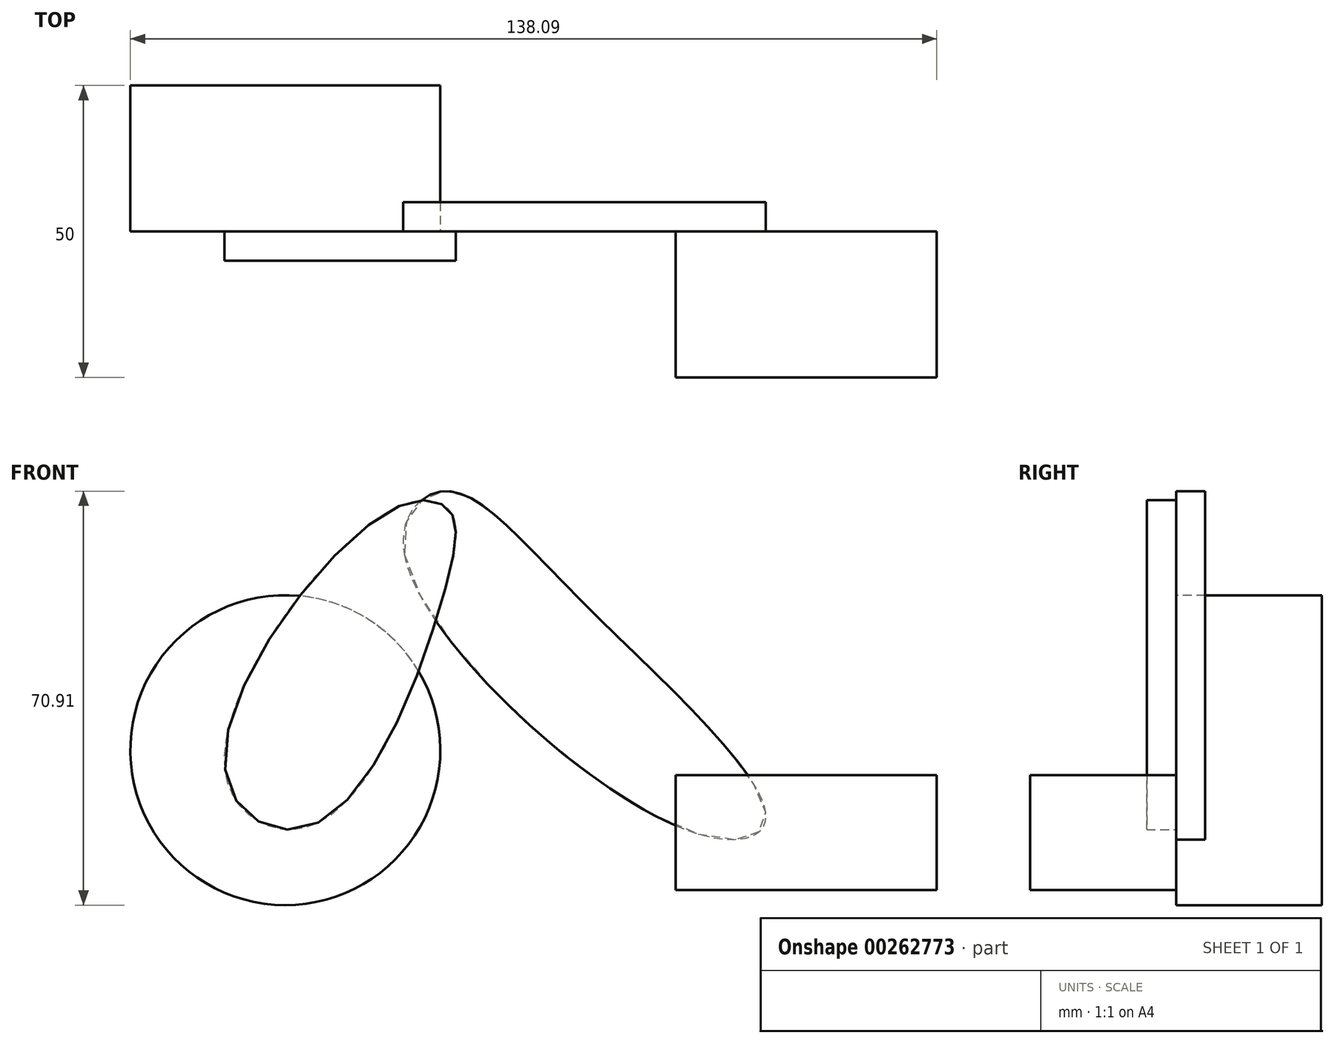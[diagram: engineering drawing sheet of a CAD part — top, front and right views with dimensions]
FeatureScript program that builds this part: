
annotation { "Feature Type Name" : "Feature", "Feature Type Description" : "" }
export const myFeature = defineFeature(function(context is Context, id is Id, definition is map)
    precondition{}
    {
        {
            var Q0;
            Q0=qCreatedBy(makeId("Front.planeOp"),FACE);
            var sketch = newSketch(context, id + "F0", { "sketchPlane" : qUnion([Q0])});
            skCircle(sketch, "E0", {"center": v(0, 0) * mm, "radius": 26.54 * mm});
            skSolve(sketch);
        }
        {
            var Q0;
            Q0=qCreatedBy(makeId("Front.planeOp"),FACE);
            var sketch = newSketch(context, id + "F1", { "sketchPlane" : qUnion([Q0])});
            skFitSpline(sketch, "E1", {"points": [v(-10.32, -3.32) * mm, v(17.7, 40.91) * mm, v(28.01, 41.16) * mm, v(27.77, 29.12) * mm, v(5.16, -12.65) * mm, v(-10.32, -3.32) * mm]});
            skSolve(sketch);
        }
        {
            var Q0;
            Q0=qCreatedBy(makeId("Front.planeOp"),FACE);
            var sketch = newSketch(context, id + "F2", { "sketchPlane" : qUnion([Q0])});
            skFitSpline(sketch, "E2", {"points": [v(20.4, 33.54) * mm, v(69.3, -13.88) * mm, v(82.31, -11.43) * mm, v(49.63, 26.66) * mm, v(27.03, 44.35) * mm, v(20.4, 33.54) * mm]});
            skSolve(sketch);
        }
        {
            var Q0;
            Q0=qCreatedBy(makeId("Front.planeOp"),FACE);
            var sketch = newSketch(context, id + "F3", { "sketchPlane" : qUnion([Q0])});
            skLineSegment(sketch, "E3.bottom", {"start": v(66.83, -23.96) * mm, "end": v(111.55, -23.96) * mm});
            skLineSegment(sketch, "E3.top", {"start": v(66.83, -4.3) * mm, "end": v(111.55, -4.3) * mm});
            skLineSegment(sketch, "E3.left", {"start": v(66.83, -23.96) * mm, "end": v(66.83, -4.3) * mm});
            skLineSegment(sketch, "E3.right", {"start": v(111.55, -23.96) * mm, "end": v(111.55, -4.3) * mm});
            skSolve(sketch);
        }
        {
            var Q0;
            Q0=makeQuery(id+"F0.imprint","IMPRINT",FACE,{"disambiguationData":[TD([[makeQuery(id+"F0.imprint","IMPRINT",EDGE,{"derivedFrom":sQuery(id+"F0.wireOp",EDGE,"E0")}),1.0]])]});
            extrude(context, id + "F4", {"entities" : qUnion([Q0]), "oppositeDirection" : true, "depth" : 25 * mm});
        }
        {
            var Q0;
            Q0=makeQuery(id+"F1.imprint","IMPRINT",FACE,{"disambiguationData":[TD([[makeQuery(id+"F1.imprint","IMPRINT",EDGE,{"derivedFrom":sQuery(id+"F1.wireOp",EDGE,"E1")}),-1.0]])]});
            var Q1;
            Q1=sQuery(id+"F1.wireOp",EDGE,"E1");
            extrude(context, id + "F5", {"entities" : qUnion([Q0]), "surfaceEntities" : qUnion([Q1]), "depth" : 5 * mm});
        }
        {
            var Q0;
            Q0=makeQuery(id+"F2.imprint","IMPRINT",FACE,{"disambiguationData":[TD([[makeQuery(id+"F2.imprint","IMPRINT",EDGE,{"derivedFrom":sQuery(id+"F2.wireOp",EDGE,"E2")}),1.0]])]});
            extrude(context, id + "F6", {"entities" : qUnion([Q0]), "operationType" : NewBodyOperationType.ADD, "oppositeDirection" : true, "depth" : 5 * mm});
        }
        {
            var Q0;
            Q0=makeQuery(id+"F3.imprint","IMPRINT",FACE,{"disambiguationData":[TD([[makeQuery(id+"F3.imprint","IMPRINT",EDGE,{"derivedFrom":sQuery(id+"F3.wireOp",EDGE,"E3.bottom")}),1.0]])]});
            extrude(context, id + "F7", {"entities" : qUnion([Q0]), "depth" : 25 * mm});
        }
    });
